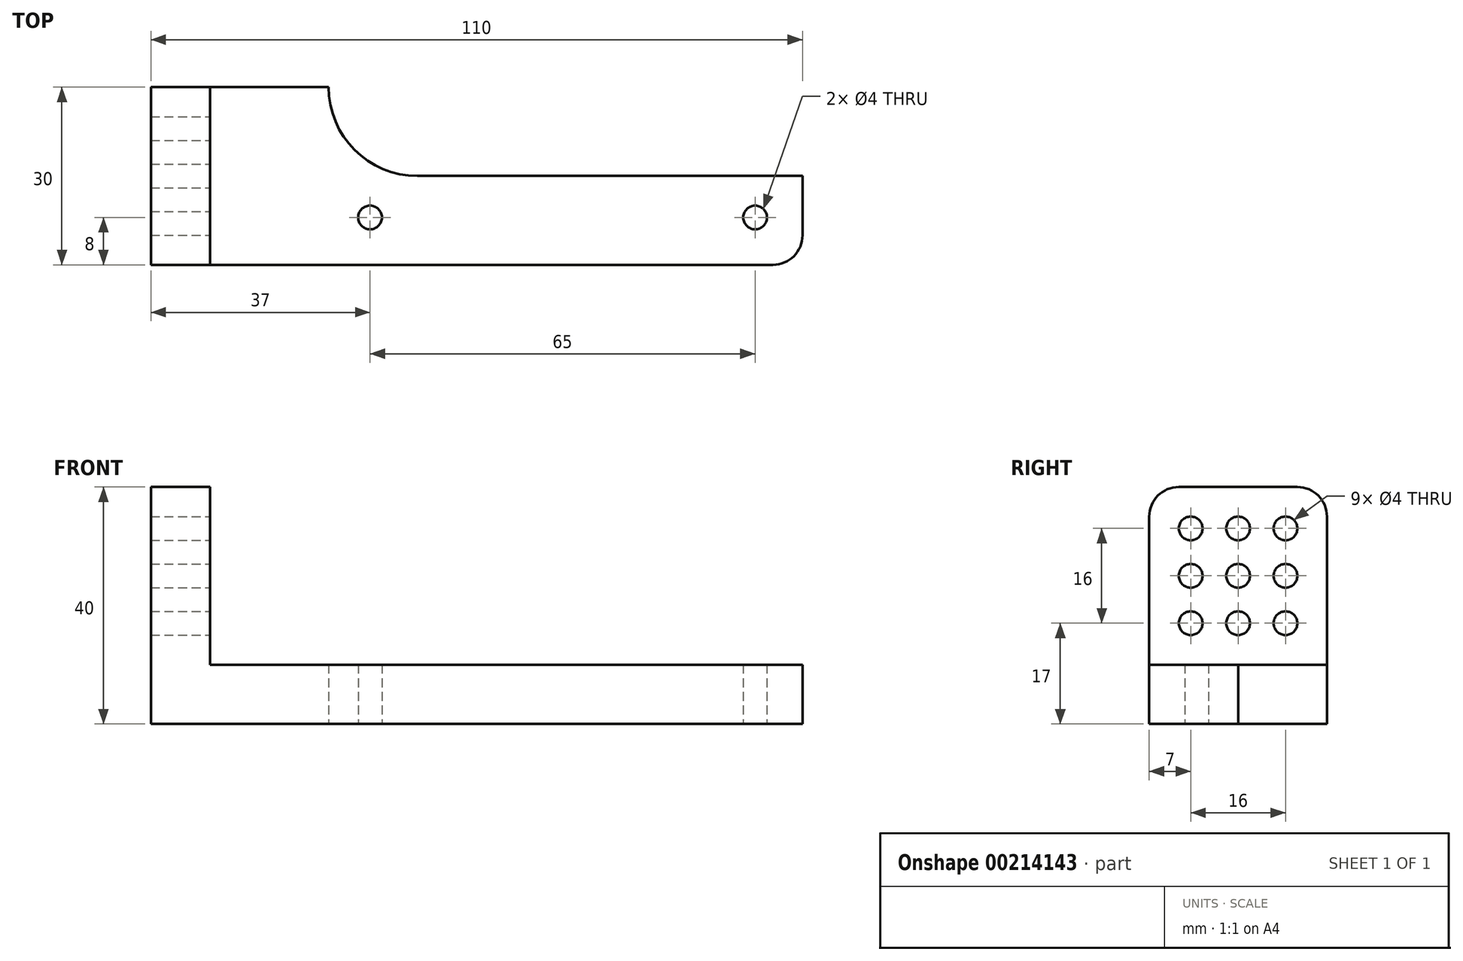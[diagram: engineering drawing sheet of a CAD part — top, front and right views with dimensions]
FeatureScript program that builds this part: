
annotation { "Feature Type Name" : "Feature", "Feature Type Description" : "" }
export const myFeature = defineFeature(function(context is Context, id is Id, definition is map)
    precondition{}
    {
        {
            var Q0;
            Q0=qCreatedBy(makeId("Top.planeOp"),FACE);
            var sketch = newSketch(context, id + "F0", { "sketchPlane" : qUnion([Q0])});
            skLineSegment(sketch, "E0.bottom", {"start": v(0, 0) * mm, "end": v(-110, 0) * mm});
            skLineSegment(sketch, "E0.top", {"start": v(0, 30) * mm, "end": v(-110, 30) * mm});
            skLineSegment(sketch, "E0.left", {"start": v(0, 0) * mm, "end": v(0, 30) * mm});
            skLineSegment(sketch, "E0.right", {"start": v(-110, 0) * mm, "end": v(-110, 30) * mm});
            skSolve(sketch);
        }
        {
            var Q0;
            Q0=makeQuery(id+"F0.imprint","IMPRINT",FACE,{"disambiguationData":[TD([[makeQuery(id+"F0.imprint","IMPRINT",EDGE,{"derivedFrom":sQuery(id+"F0.wireOp",EDGE,"E0.bottom")}),-1.0]])]});
            extrude(context, id + "F1", {"entities" : qUnion([Q0]), "depth" : 10 * mm});
        }
        {
            var Q0;
            Q0=makeQuery(id+"F1.opExtrude","CAP_FACE",FACE,{"disambiguationData":[OSD([sQuery(id+"F0.wireOp",EDGE,"E0.bottom"),sQuery(id+"F0.wireOp",EDGE,"E0.top"),sQuery(id+"F0.wireOp",EDGE,"E0.left"),sQuery(id+"F0.wireOp",EDGE,"E0.right")])],"isStart":true});
            var sketch = newSketch(context, id + "F2", { "sketchPlane" : qUnion([Q0])});
            skCircle(sketch, "E1", {"center": v(-8, -8) * mm, "radius": 2 * mm});
            skCircle(sketch, "E2", {"center": v(-73, -8) * mm, "radius": 2 * mm});
            skLineSegment(sketch, "E3", {"start": v(0, -15) * mm, "end": v(-80, -15) * mm});
            skArc(sketch, "E4", {"start": v(-65, -15) * mm, "mid": v(-75.6, -19.4) * mm, "end": v(-80, -30) * mm});
            skSolve(sketch);
        }
        {
            var Q0;
            {var subQ0=sQuery(id+"F2.wireOp",EDGE,"fuIlYsDQ-MXDi-Gm20-4fFZ-zyXwgk5qTBZB");Q0=makeQuery(id+"F2.imprint","IMPRINT",FACE,{"disambiguationData":[TD([[makeQuery(id+"F2.imprint","IMPRINT",EDGE,{"derivedFrom":subQ0}),1.0]])]});}
            var Q1;
            Q1=makeQuery(id+"F2.imprint","IMPRINT",FACE,{"disambiguationData":[TD([[makeQuery(id+"F2.imprint","IMPRINT",EDGE,{"derivedFrom":sQuery(id+"F2.wireOp",EDGE,"E1")}),1.0]])]});
            var Q2;
            Q2=makeQuery(id+"F2.imprint","IMPRINT",FACE,{"disambiguationData":[TD([[makeQuery(id+"F2.imprint","IMPRINT",EDGE,{"derivedFrom":sQuery(id+"F2.wireOp",EDGE,"E2")}),1.0]])]});
            var Q3;
            {var subQ3=sQuery(id+"F2.wireOp",EDGE,"ZSO6Oc9X-E8c2-FxbR-L1og-qFMxZH5hB1vx");Q3=makeQuery(id+"F2.imprint","IMPRINT",FACE,{"disambiguationData":[TD([[makeQuery(id+"F2.imprint","IMPRINT",EDGE,{"derivedFrom":subQ3}),1.0]])]});}
            var Q4;
            {var subQ3=sQuery(id+"F2.wireOp",EDGE,"E4");Q4=makeQuery(id+"F2.imprint","IMPRINT",FACE,{"disambiguationData":[TD([[makeQuery(id+"F2.imprint","IMPRINT",EDGE,{"derivedFrom":subQ3}),1.0]])]});}
            extrude(context, id + "F3", {"entities" : qUnion([Q0, Q1, Q2, Q3, Q4]), "operationType" : NewBodyOperationType.REMOVE, "oppositeDirection" : true, "depth" : 25 * mm});
        }
        {
            var Q0;
            Q0=makeQuery(id+"F1.opExtrude","CAP_FACE",FACE,{"disambiguationData":[OSD([sQuery(id+"F0.wireOp",EDGE,"E0.bottom"),sQuery(id+"F0.wireOp",EDGE,"E0.top"),sQuery(id+"F0.wireOp",EDGE,"E0.left"),sQuery(id+"F0.wireOp",EDGE,"E0.right")])],"isStart":false});
            var sketch = newSketch(context, id + "F4", { "sketchPlane" : qUnion([Q0])});
            skLineSegment(sketch, "E5", {"start": v(-100, 0) * mm, "end": v(-100, 30) * mm});
            skSolve(sketch);
        }
        {
            var Q0;
            {var subQ0=sQuery(id+"F4.wireOp",EDGE,"E5");Q0=makeQuery(id+"F4.imprint","IMPRINT",FACE,{"disambiguationData":[TD([[makeQuery(id+"F4.imprint","IMPRINT",EDGE,{"derivedFrom":subQ0}),1.0]])]});}
            extrude(context, id + "F5", {"entities" : qUnion([Q0]), "operationType" : NewBodyOperationType.ADD, "depth" : 30 * mm});
        }
        {
            var Q0;
            Q0=makeQuery(id+"F5.opExtrude","SWEPT_FACE",FACE,{"disambiguationData":[OSD([sQuery(id+"F4.wireOp",EDGE,"E5")])]});
            var sketch = newSketch(context, id + "F6", { "sketchPlane" : qUnion([Q0])});
            skCircle(sketch, "E6", {"center": v(7, 17) * mm, "radius": 2 * mm});
            skCircle(sketch, "E7", {"center": v(7, 25) * mm, "radius": 2 * mm});
            skCircle(sketch, "E8", {"center": v(7, 33) * mm, "radius": 2 * mm});
            skCircle(sketch, "E9", {"center": v(15, 33) * mm, "radius": 2 * mm});
            skCircle(sketch, "E10", {"center": v(23, 33) * mm, "radius": 2 * mm});
            skCircle(sketch, "E11", {"center": v(23, 25) * mm, "radius": 2 * mm});
            skCircle(sketch, "E12", {"center": v(15, 25) * mm, "radius": 2 * mm});
            skCircle(sketch, "E13", {"center": v(15, 17) * mm, "radius": 2 * mm});
            skCircle(sketch, "E14", {"center": v(23, 17) * mm, "radius": 2 * mm});
            skSolve(sketch);
        }
        {
            var Q0;
            Q0=makeQuery(id+"F6.imprint","IMPRINT",FACE,{"disambiguationData":[TD([[makeQuery(id+"F6.imprint","IMPRINT",EDGE,{"derivedFrom":sQuery(id+"F6.wireOp",EDGE,"E6")}),1.0]])]});
            var Q1;
            Q1=makeQuery(id+"F6.imprint","IMPRINT",FACE,{"disambiguationData":[TD([[makeQuery(id+"F6.imprint","IMPRINT",EDGE,{"derivedFrom":sQuery(id+"F6.wireOp",EDGE,"E7")}),1.0]])]});
            var Q2;
            Q2=makeQuery(id+"F6.imprint","IMPRINT",FACE,{"disambiguationData":[TD([[makeQuery(id+"F6.imprint","IMPRINT",EDGE,{"derivedFrom":sQuery(id+"F6.wireOp",EDGE,"E9")}),1.0]])]});
            var Q3;
            Q3=makeQuery(id+"F6.imprint","IMPRINT",FACE,{"disambiguationData":[TD([[makeQuery(id+"F6.imprint","IMPRINT",EDGE,{"derivedFrom":sQuery(id+"F6.wireOp",EDGE,"E8")}),1.0]])]});
            var Q4;
            Q4=makeQuery(id+"F6.imprint","IMPRINT",FACE,{"disambiguationData":[TD([[makeQuery(id+"F6.imprint","IMPRINT",EDGE,{"derivedFrom":sQuery(id+"F6.wireOp",EDGE,"E12")}),1.0]])]});
            var Q5;
            Q5=makeQuery(id+"F6.imprint","IMPRINT",FACE,{"disambiguationData":[TD([[makeQuery(id+"F6.imprint","IMPRINT",EDGE,{"derivedFrom":sQuery(id+"F6.wireOp",EDGE,"E13")}),1.0]])]});
            var Q6;
            Q6=makeQuery(id+"F6.imprint","IMPRINT",FACE,{"disambiguationData":[TD([[makeQuery(id+"F6.imprint","IMPRINT",EDGE,{"derivedFrom":sQuery(id+"F6.wireOp",EDGE,"E14")}),1.0]])]});
            var Q7;
            Q7=makeQuery(id+"F6.imprint","IMPRINT",FACE,{"disambiguationData":[TD([[makeQuery(id+"F6.imprint","IMPRINT",EDGE,{"derivedFrom":sQuery(id+"F6.wireOp",EDGE,"E11")}),1.0]])]});
            var Q8;
            Q8=makeQuery(id+"F6.imprint","IMPRINT",FACE,{"disambiguationData":[TD([[makeQuery(id+"F6.imprint","IMPRINT",EDGE,{"derivedFrom":sQuery(id+"F6.wireOp",EDGE,"E10")}),1.0]])]});
            extrude(context, id + "F7", {"entities" : qUnion([Q0, Q1, Q2, Q3, Q4, Q5, Q6, Q7, Q8]), "operationType" : NewBodyOperationType.REMOVE, "oppositeDirection" : true, "depth" : 25 * mm});
        }
        {
            var Q0;
            Q0=makeQuery(id+"F3.boolean.opBoolean","COPY",EDGE,{"derivedFrom":makeQuery(id+"F3.opExtrude","SWEPT_EDGE",EDGE,{"disambiguationData":[OSD([sQuery(id+"F0.wireOp",EDGE,"E0.left"),sQuery(id+"F2.wireOp",EDGE,"E3")])]})});
            var Q1;
            Q1=makeQuery(id+"F1.opExtrude","SWEPT_EDGE",EDGE,{"disambiguationData":[OSD([sQuery(id+"F0.wireOp",EDGE,"E0.bottom"),sQuery(id+"F0.wireOp",EDGE,"E0.left")])]});
            var Q2;
            Q2=makeQuery(id+"F3.boolean.opBoolean","COPY",EDGE,{"derivedFrom":makeQuery(id+"F3.opExtrude","SWEPT_EDGE",EDGE,{"disambiguationData":[OSD([sQuery(id+"F0.wireOp",EDGE,"E0.top"),sQuery(id+"F2.wireOp",EDGE,"E4")])]})});
            var Q3;
            Q3=makeQuery(id+"F5.opExtrude","CAP_EDGE",EDGE,{"disambiguationData":[OSD([sQuery(id+"F0.wireOp",EDGE,"E0.top")])],"isStart":false});
            var Q4;
            Q4=makeQuery(id+"F5.opExtrude","CAP_EDGE",EDGE,{"disambiguationData":[OSD([sQuery(id+"F0.wireOp",EDGE,"E0.bottom")])],"isStart":false});
            var Q5;
            Q5=makeQuery(id+"F5.opExtrude","CAP_EDGE",EDGE,{"disambiguationData":[OSD([sQuery(id+"F4.wireOp",EDGE,"E5")])],"isStart":true});
            fillet(context, id + "F8", {"entities" : qUnion([Q0, Q1, Q2, Q3, Q4, Q5]), "radius" : 5 * mm, "tangentPropagation" : true, "allowEdgeOverflow" : false});
        }
    });
